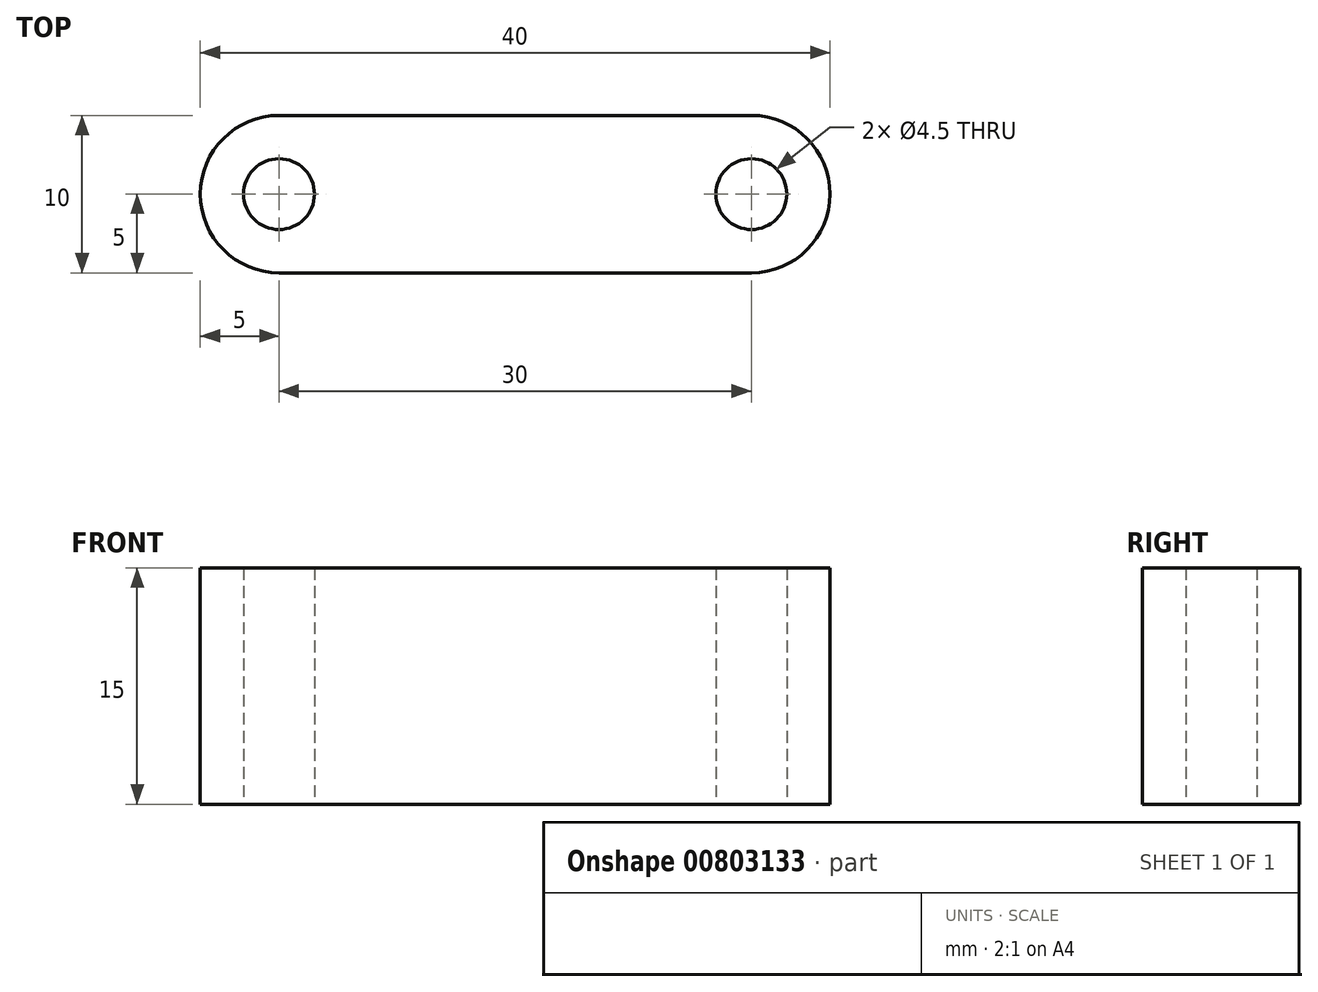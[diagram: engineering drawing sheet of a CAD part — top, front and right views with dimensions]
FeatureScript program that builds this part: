
annotation { "Feature Type Name" : "Feature", "Feature Type Description" : "" }
export const myFeature = defineFeature(function(context is Context, id is Id, definition is map)
    precondition{}
    {
        {
            var Q0;
            Q0=qCreatedBy(makeId("Top.planeOp"),FACE);
            var sketch = newSketch(context, id + "F0", { "sketchPlane" : qUnion([Q0])});
            skLineSegment(sketch, "E0.bottom", {"start": v(15, 5) * mm, "end": v(-15, 5) * mm});
            skLineSegment(sketch, "E0.top", {"start": v(15, -5) * mm, "end": v(-15, -5) * mm});
            skLineSegment(sketch, "E0.left", {"start": v(20, 0) * mm, "end": v(20, 0) * mm});
            skLineSegment(sketch, "E0.right", {"start": v(-20, 0) * mm, "end": v(-20, 0) * mm});
            skPoint(sketch, "E0.middle", {"position": v(0, 0) * mm});
            skCircle(sketch, "E1", {"center": v(-15, 0) * mm, "radius": 2.25 * mm});
            skCircle(sketch, "E2", {"center": v(15, 0) * mm, "radius": 2.25 * mm});
            skPoint(sketch, "E3.visualSharp", {"position": v(-20, 5) * mm});
            skArc(sketch, "E3.filletArc", {"start": v(-15, 5) * mm, "mid": v(-18.54, 3.54) * mm, "end": v(-20, 0) * mm});
            skPoint(sketch, "E4.visualSharp", {"position": v(-20, -5) * mm});
            skArc(sketch, "E4.filletArc", {"start": v(-20, 0) * mm, "mid": v(-18.54, -3.54) * mm, "end": v(-15, -5) * mm});
            skPoint(sketch, "E5.visualSharp", {"position": v(20, -5) * mm});
            skArc(sketch, "E5.filletArc", {"start": v(15, -5) * mm, "mid": v(18.54, -3.54) * mm, "end": v(20, 0) * mm});
            skPoint(sketch, "E6.visualSharp", {"position": v(20, 5) * mm});
            skArc(sketch, "E6.filletArc", {"start": v(20, 0) * mm, "mid": v(18.54, 3.54) * mm, "end": v(15, 5) * mm});
            skSolve(sketch);
        }
        {
            var Q0;
            Q0=makeQuery(id+"F0.imprint","IMPRINT",FACE,{"disambiguationData":[TD([[makeQuery(id+"F0.imprint","IMPRINT",EDGE,{"derivedFrom":sQuery(id+"F0.wireOp",EDGE,"E0.bottom")}),1.0]])]});
            extrude(context, id + "F1", {"entities" : qUnion([Q0]), "depth" : 15 * mm, "offsetDistance" : 25 * mm});
        }
    });
